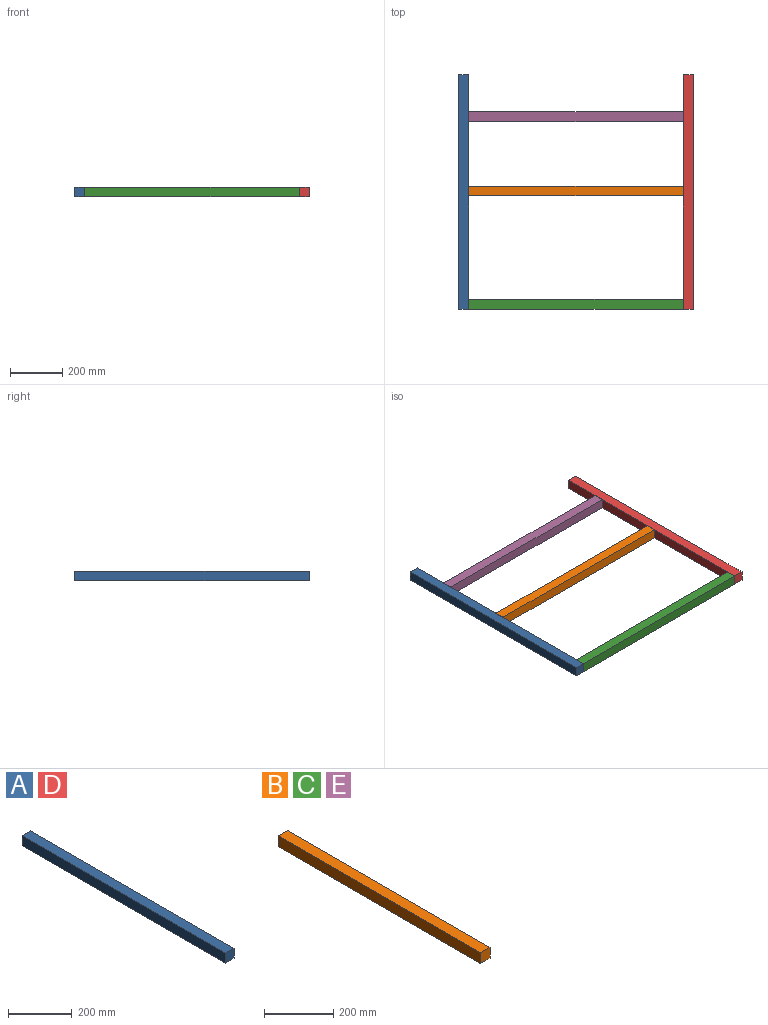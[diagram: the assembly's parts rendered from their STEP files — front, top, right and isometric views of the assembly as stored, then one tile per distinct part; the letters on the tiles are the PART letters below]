
ASSEMBLY  parts=5 mates=2
PART A: 6 faces, bbox 38.1x901.7x38.1 mm
  f0: plane 901.7x38.1mm, normal (1,0,0), area 34354.8mm2, adj f1,f3,f4,f5
  f1: plane 901.7x38.1mm, normal (0,0,1), area 34354.8mm2, adj f0,f2,f4,f5
  f2: plane 901.7x38.1mm, normal (-1,0,0), area 34354.8mm2, adj f1,f3,f4,f5
  f3: plane 901.7x38.1mm, normal (0,0,-1), area 34354.8mm2, adj f0,f2,f4,f5
  f4: plane 38.1x38.1mm, normal (0,-1,0), area 1451.6mm2, adj f0,f1,f2,f3
  f5: plane 38.1x38.1mm, normal (0,1,0), area 1451.6mm2, adj f0,f1,f2,f3
PART B: 6 faces, bbox 38.1x825.5x38.1 mm
  f0: plane 825.5x38.1mm, normal (1,0,0), area 31451.5mm2, adj f1,f3,f4,f5
  f1: plane 825.5x38.1mm, normal (0,0,1), area 31451.5mm2, adj f0,f2,f4,f5
  f2: plane 825.5x38.1mm, normal (-1,0,0), area 31451.5mm2, adj f1,f3,f4,f5
  f3: plane 825.5x38.1mm, normal (0,0,-1), area 31451.5mm2, adj f0,f2,f4,f5
  f4: plane 38.1x38.1mm, normal (0,-1,0), area 1451.6mm2, adj f0,f1,f2,f3
  f5: plane 38.1x38.1mm, normal (0,1,0), area 1451.6mm2, adj f0,f1,f2,f3
PART C: same geometry as B
PART D: same geometry as A
PART E: same geometry as B
PLACE A rot(axis=(0,-1,0),180deg) t=(-1.16,862.14,-18.35)mm fixed
PLACE B rot(axis=(0.58,-0.58,0.58),120deg) t=(17.89,415.09,-18.35)mm
PLACE C rot(axis=(0.58,-0.58,0.58),120deg) t=(17.59,-20.81,-18.35)mm fixed
PLACE D rot(axis=(-0.71,0,-0.71),180deg) t=(862.44,-39.56,-18.35)mm
PLACE E rot(axis=(0.58,-0.58,0.58),120deg) t=(17.89,699.58,-18.35)mm
MATE fastened A.f2 <-> B.f5  axis (1,0,0) through (17.89,415.09,-18.35)mm
MATE fastened A.f2 <-> E.f5  axis (1,0,0) through (17.89,699.58,-18.35)mm
